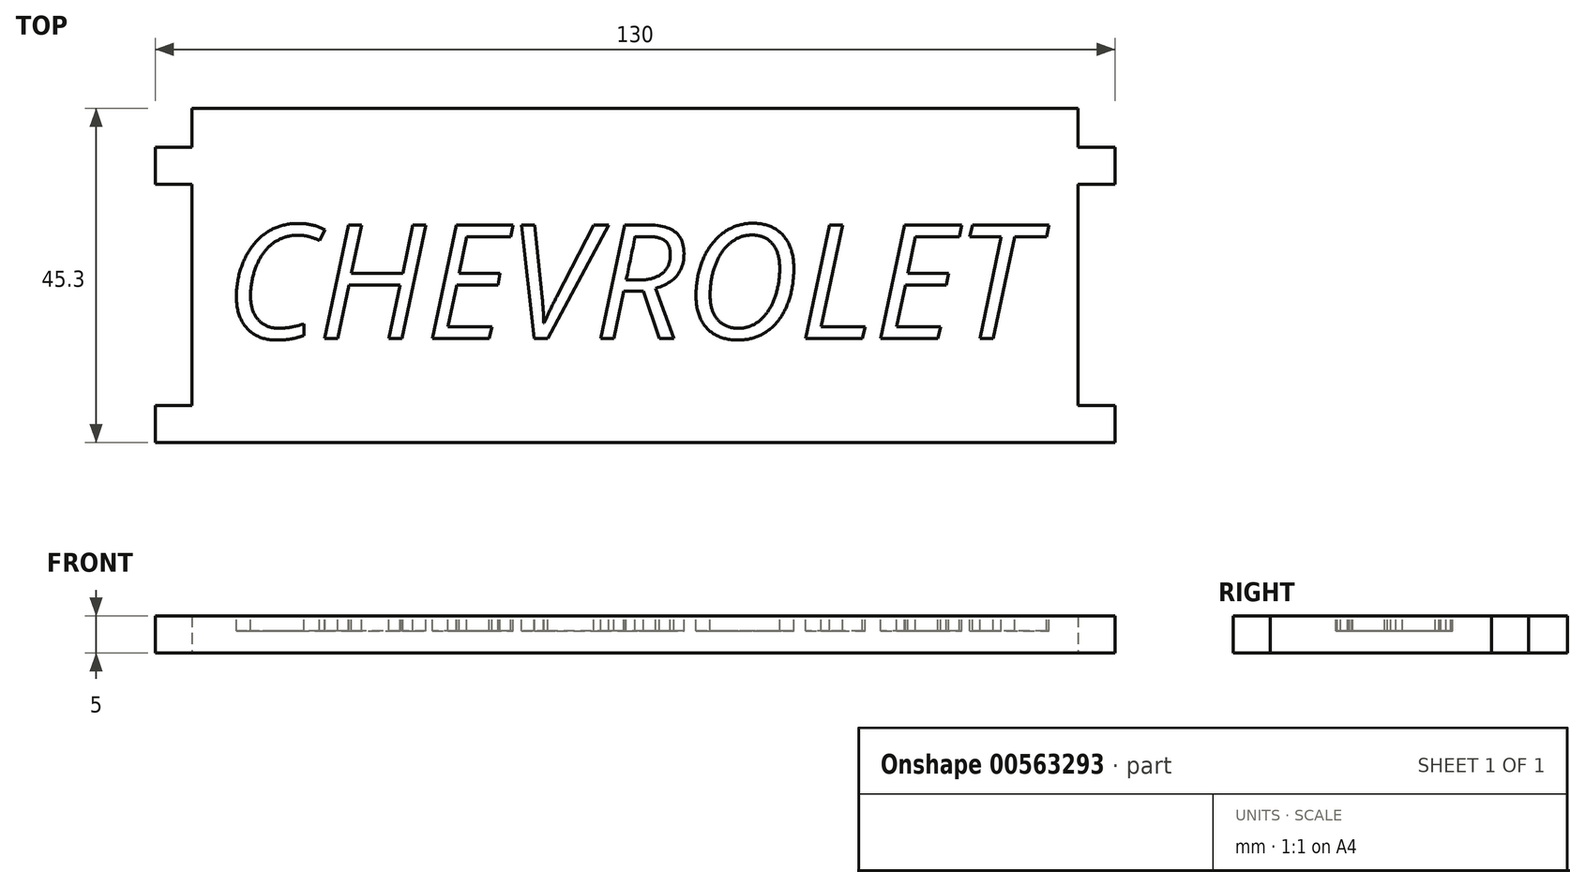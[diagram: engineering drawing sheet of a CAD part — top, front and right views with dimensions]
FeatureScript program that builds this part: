
annotation { "Feature Type Name" : "Feature", "Feature Type Description" : "" }
export const myFeature = defineFeature(function(context is Context, id is Id, definition is map)
    precondition{}
    {
        {
            var Q0;
            Q0=qCreatedBy(makeId("Top.planeOp"),FACE);
            var sketch = newSketch(context, id + "F0", { "sketchPlane" : qUnion([Q0])});
            skLineSegment(sketch, "E0.bottom", {"start": v(60, 22.65) * mm, "end": v(-60, 22.65) * mm});
            skLineSegment(sketch, "E0.top", {"start": v(60, -22.65) * mm, "end": v(-60, -22.65) * mm});
            skLineSegment(sketch, "E0.left", {"start": v(60, 22.65) * mm, "end": v(60, 17.35) * mm});
            skLineSegment(sketch, "E0.right", {"start": v(-60, 22.65) * mm, "end": v(-60, 17.35) * mm});
            skPoint(sketch, "E0.middle", {"position": v(0, 0) * mm});
            skLineSegment(sketch, "E1.bottom", {"start": v(-60, -22.65) * mm, "end": v(-65, -22.65) * mm});
            skLineSegment(sketch, "E1.top", {"start": v(-60, -17.65) * mm, "end": v(-65, -17.65) * mm});
            skLineSegment(sketch, "E1.right", {"start": v(-65, -22.65) * mm, "end": v(-65, -17.65) * mm});
            skLineSegment(sketch, "E2.bottom", {"start": v(60, -22.65) * mm, "end": v(65, -22.65) * mm});
            skLineSegment(sketch, "E2.top", {"start": v(60, -17.65) * mm, "end": v(65, -17.65) * mm});
            skLineSegment(sketch, "E2.right", {"start": v(65, -22.65) * mm, "end": v(65, -17.65) * mm});
            skLineSegment(sketch, "E3", {"start": v(-60, -17.65) * mm, "end": v(-60, 12.35) * mm});
            skLineSegment(sketch, "E4", {"start": v(-60, 12.35) * mm, "end": v(-60, -17.65) * mm});
            skLineSegment(sketch, "E5.bottom", {"start": v(-60, 12.35) * mm, "end": v(-65, 12.35) * mm});
            skLineSegment(sketch, "E5.top", {"start": v(-60, 17.35) * mm, "end": v(-65, 17.35) * mm});
            skLineSegment(sketch, "E5.right", {"start": v(-65, 12.35) * mm, "end": v(-65, 17.35) * mm});
            skLineSegment(sketch, "E6.bottom", {"start": v(60, 17.35) * mm, "end": v(65, 17.35) * mm});
            skLineSegment(sketch, "E6.top", {"start": v(60, 12.35) * mm, "end": v(65, 12.35) * mm});
            skLineSegment(sketch, "E6.right", {"start": v(65, 17.35) * mm, "end": v(65, 12.35) * mm});
            skLineSegment(sketch, "E7.trimOffspring", {"start": v(60, 12.35) * mm, "end": v(60, -17.65) * mm});
            skSolve(sketch);
        }
        {
            var Q0;
            Q0 = qSketchRegion(id + "F0", true);
            extrude(context, id + "F1", {"entities" : qUnion([Q0]), "depth" : 5 * mm, "offsetDistance" : 25 * mm});
        }
        {
            var Q0;
            Q0=makeQuery(id+"F1.opExtrude","CAP_FACE",FACE,{"disambiguationData":[OSD([sQuery(id+"F0.wireOp",EDGE,"E0.bottom"),sQuery(id+"F0.wireOp",EDGE,"E0.top"),sQuery(id+"F0.wireOp",EDGE,"E0.left"),sQuery(id+"F0.wireOp",EDGE,"E0.right"),sQuery(id+"F0.wireOp",EDGE,"E1.bottom"),sQuery(id+"F0.wireOp",EDGE,"E1.top"),sQuery(id+"F0.wireOp",EDGE,"E1.right"),sQuery(id+"F0.wireOp",EDGE,"E2.bottom"),sQuery(id+"F0.wireOp",EDGE,"E2.top"),sQuery(id+"F0.wireOp",EDGE,"E2.right"),sQuery(id+"F0.wireOp",EDGE,"E5.bottom"),sQuery(id+"F0.wireOp",EDGE,"E5.top"),sQuery(id+"F0.wireOp",EDGE,"E5.right"),sQuery(id+"F0.wireOp",EDGE,"E6.bottom"),sQuery(id+"F0.wireOp",EDGE,"E6.top"),sQuery(id+"F0.wireOp",EDGE,"E6.right"),sQuery(id+"F0.wireOp",EDGE,"E4"),sQuery(id+"F0.wireOp",EDGE,"E7.trimOffspring")])],"isStart":false});
            var sketch = newSketch(context, id + "F2", { "sketchPlane" : qUnion([Q0])});
            skText(sketch, "E8", { "text": "CHEVROLET", "fontName": "OpenSans-Italic.ttf"});
            const initialGuessF2  = {"E8": [-0.05558, -0.00854, 1, 0, 0.0155]};
            skSetInitialGuess(sketch, initialGuessF2);
            skSolve(sketch);
        }
        {
            var Q0;
            Q0 = qSketchRegion(id + "F2", true);
            extrude(context, id + "F3", {"entities" : qUnion([Q0]), "operationType" : NewBodyOperationType.REMOVE, "oppositeDirection" : true, "depth" : 2 * mm, "offsetDistance" : 25 * mm});
        }
    });
